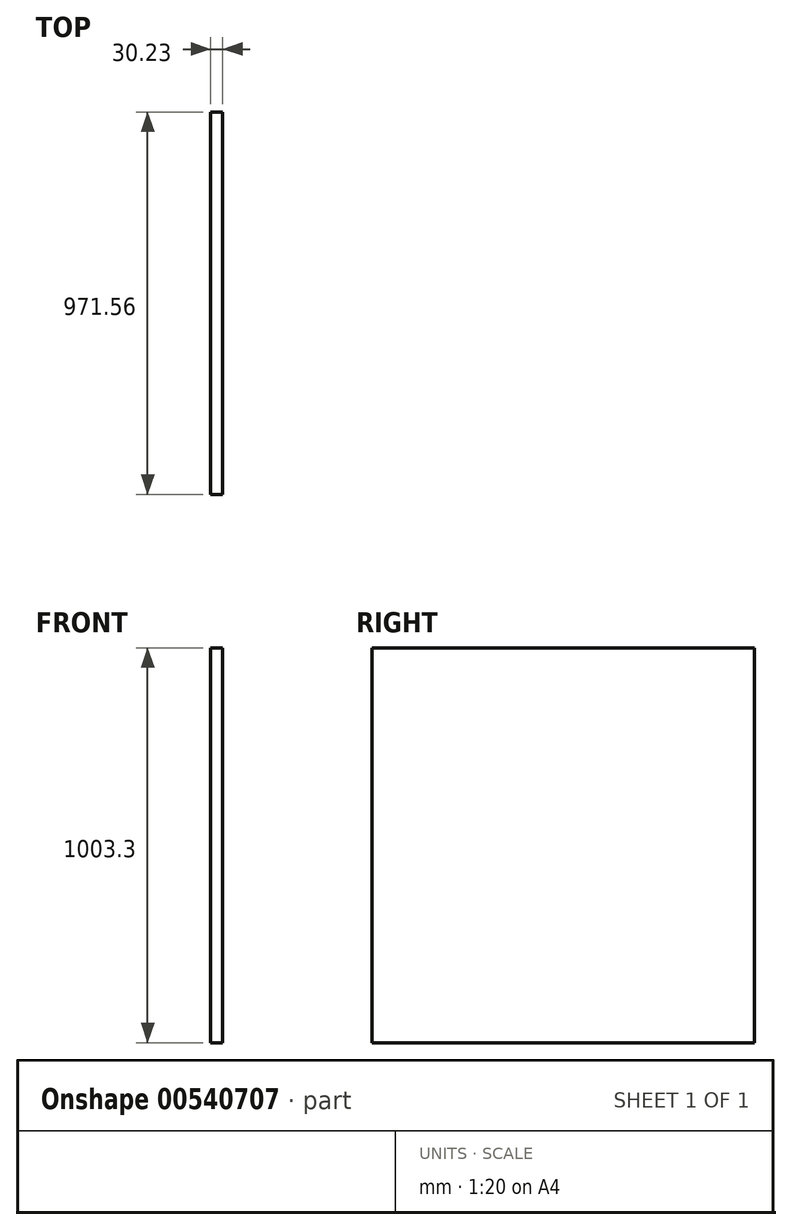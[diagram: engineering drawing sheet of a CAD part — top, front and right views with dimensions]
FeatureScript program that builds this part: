
annotation { "Feature Type Name" : "Feature", "Feature Type Description" : "" }
export const myFeature = defineFeature(function(context is Context, id is Id, definition is map)
    precondition{}
    {
        {
            var Q0;
            Q0=qCreatedBy(makeId("Right.planeOp"),FACE);
            var sketch = newSketch(context, id + "F0", { "sketchPlane" : qUnion([Q0])});
            skLineSegment(sketch, "E0.bottom", {"start": v(485.77, 501.65) * mm, "end": v(-485.78, 501.65) * mm});
            skLineSegment(sketch, "E0.top", {"start": v(485.78, -501.65) * mm, "end": v(-485.77, -501.65) * mm});
            skLineSegment(sketch, "E0.left", {"start": v(485.77, 501.65) * mm, "end": v(485.78, -501.65) * mm});
            skLineSegment(sketch, "E0.right", {"start": v(-485.78, 501.65) * mm, "end": v(-485.77, -501.65) * mm});
            skPoint(sketch, "E0.middle", {"position": v(0, 0) * mm});
            skSolve(sketch);
        }
        {
            var Q0;
            Q0=makeQuery(id+"F0.imprint","IMPRINT",FACE,{"disambiguationData":[TD([[makeQuery(id+"F0.imprint","IMPRINT",EDGE,{"derivedFrom":sQuery(id+"F0.wireOp",EDGE,"E0.bottom")}),1.0]])]});
            extrude(context, id + "F1", {"entities" : qUnion([Q0]), "depth" : 30.23 * mm, "offsetDistance" : 25.4 * mm});
        }
    });
